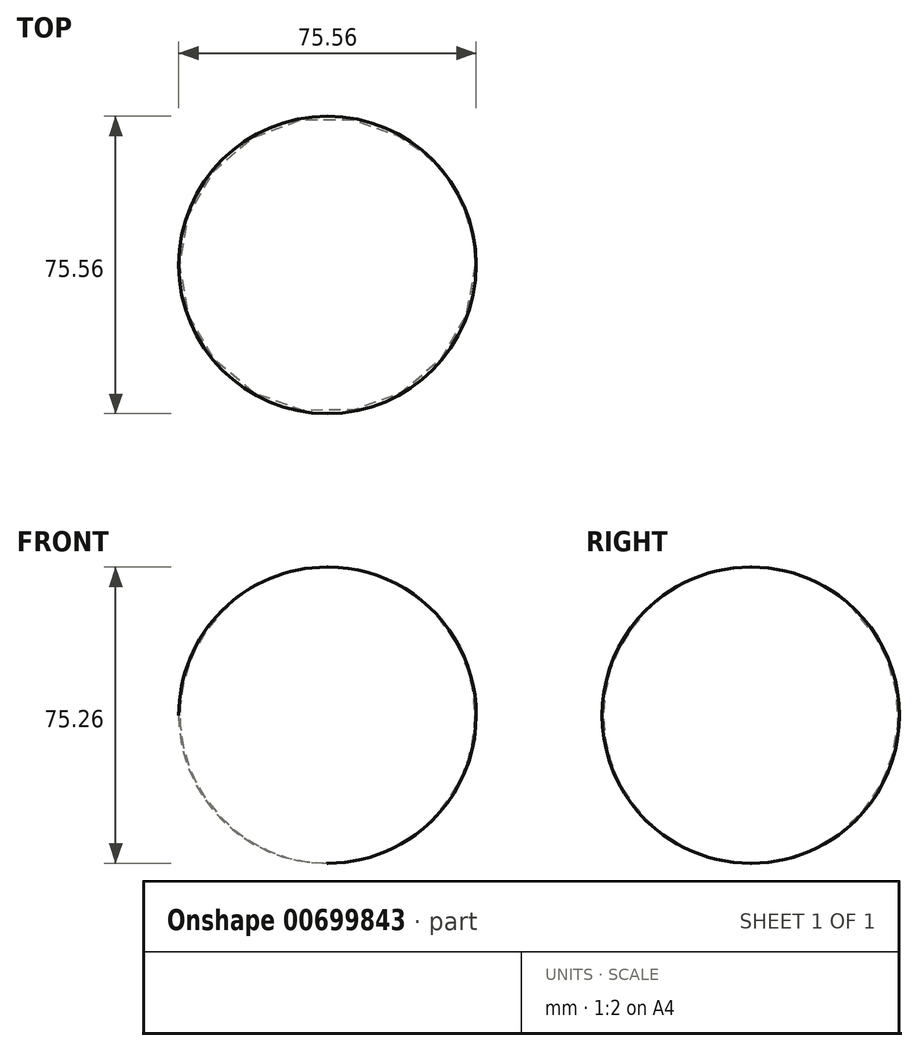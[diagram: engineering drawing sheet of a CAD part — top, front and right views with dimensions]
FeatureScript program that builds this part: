
annotation { "Feature Type Name" : "Feature", "Feature Type Description" : "" }
export const myFeature = defineFeature(function(context is Context, id is Id, definition is map)
    precondition{}
    {
        {
            var Q0;
            Q0=qCreatedBy(makeId("Front.planeOp"),FACE);
            var sketch = newSketch(context, id + "F0", { "sketchPlane" : qUnion([Q0])});
            skLineSegment(sketch, "E0", {"start": v(0, 0) * mm, "end": v(0, 75.26) * mm});
            skArc(sketch, "E1", {"start": v(0, 75.26) * mm, "mid": v(-37.78, 37.63) * mm, "end": v(0, 0) * mm});
            skSolve(sketch);
        }
        {
            var Q0;
            Q0=makeQuery(id+"F0.imprint","IMPRINT",FACE,{"disambiguationData":[TD([[makeQuery(id+"F0.imprint","IMPRINT",EDGE,{"derivedFrom":sQuery(id+"F0.wireOp",EDGE,"E0")}),1.0]])]});
            var Q1;
            Q1=sQuery(id+"F0.wireOp",EDGE,"E0");
            revolve(context, id + "F1", {"entities" : qUnion([Q0]), "axis" : qUnion([Q1]), "revolveType" : RevolveType.FULL});
        }
    });
